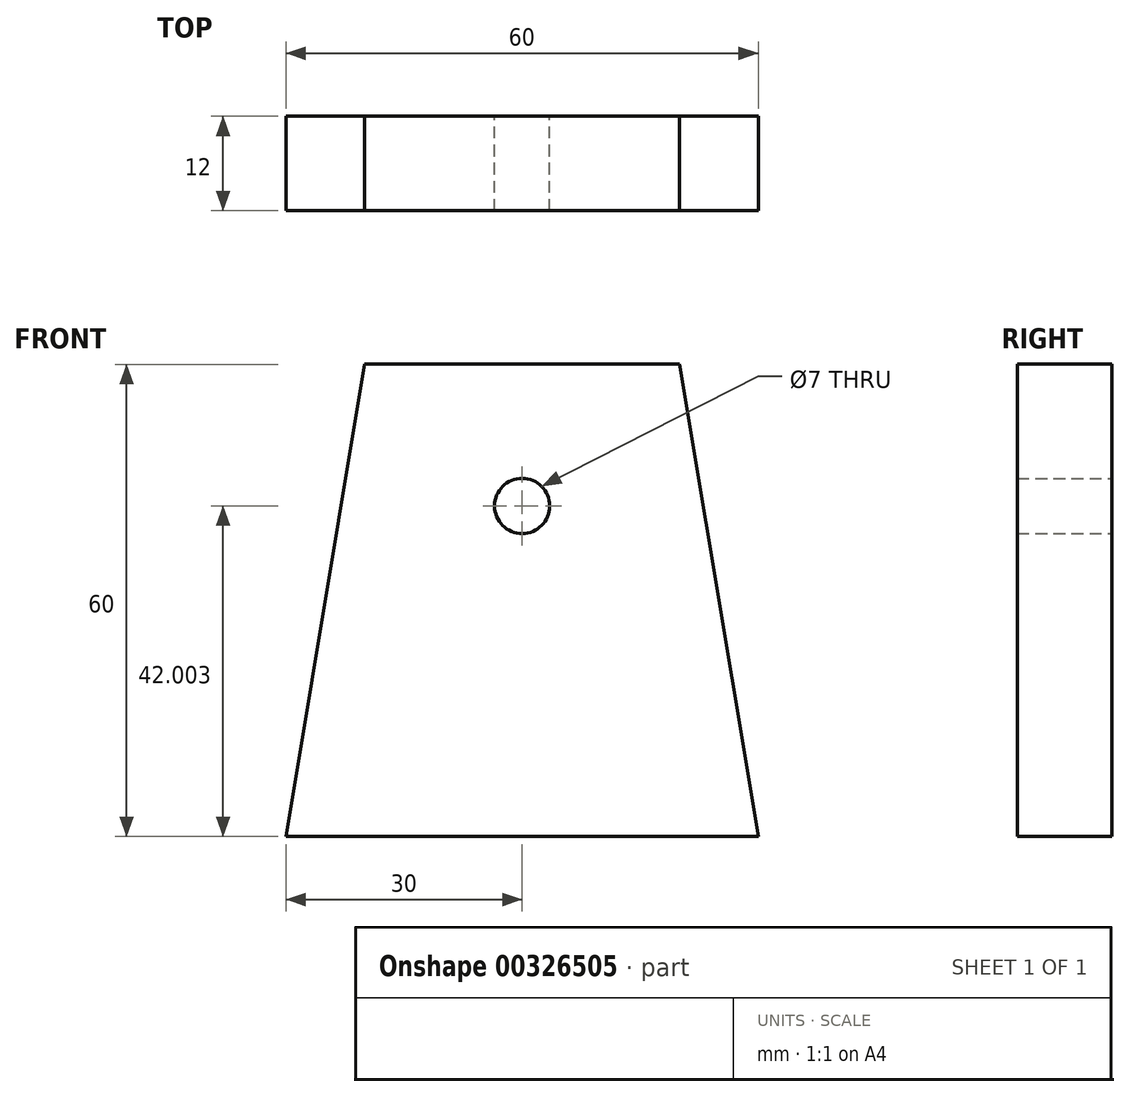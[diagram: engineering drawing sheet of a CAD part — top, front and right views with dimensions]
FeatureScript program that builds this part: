
annotation { "Feature Type Name" : "Feature", "Feature Type Description" : "" }
export const myFeature = defineFeature(function(context is Context, id is Id, definition is map)
    precondition{}
    {
        {
            var Q0;
            Q0=qCreatedBy(makeId("Front.planeOp"),FACE);
            var sketch = newSketch(context, id + "F0", { "sketchPlane" : qUnion([Q0])});
            skLineSegment(sketch, "E0", {"start": v(-50, -48.74) * mm, "end": v(10, -48.74) * mm});
            skLineSegment(sketch, "E1", {"start": v(0, 11.26) * mm, "end": v(-40, 11.26) * mm});
            skLineSegment(sketch, "E2", {"start": v(-40, 11.26) * mm, "end": v(-50, -48.74) * mm});
            skLineSegment(sketch, "E3", {"start": v(0, 11.26) * mm, "end": v(10, -48.74) * mm});
            skLineSegment(sketch, "E4", {"start": v(-20, -48.74) * mm, "end": v(-20, -6.74) * mm, "construction": true});
            skCircle(sketch, "E5", {"center": v(-20, -6.74) * mm, "radius": 3.5 * mm});
            skSolve(sketch);
        }
        {
            var Q0;
            Q0=makeQuery(id+"F0.imprint","IMPRINT",FACE,{"disambiguationData":[TD([[makeQuery(id+"F0.imprint","IMPRINT",EDGE,{"derivedFrom":sQuery(id+"F0.wireOp",EDGE,"E0")}),1.0]])]});
            extrude(context, id + "F1", {"entities" : qUnion([Q0]), "depth" : 12 * mm});
        }
    });
